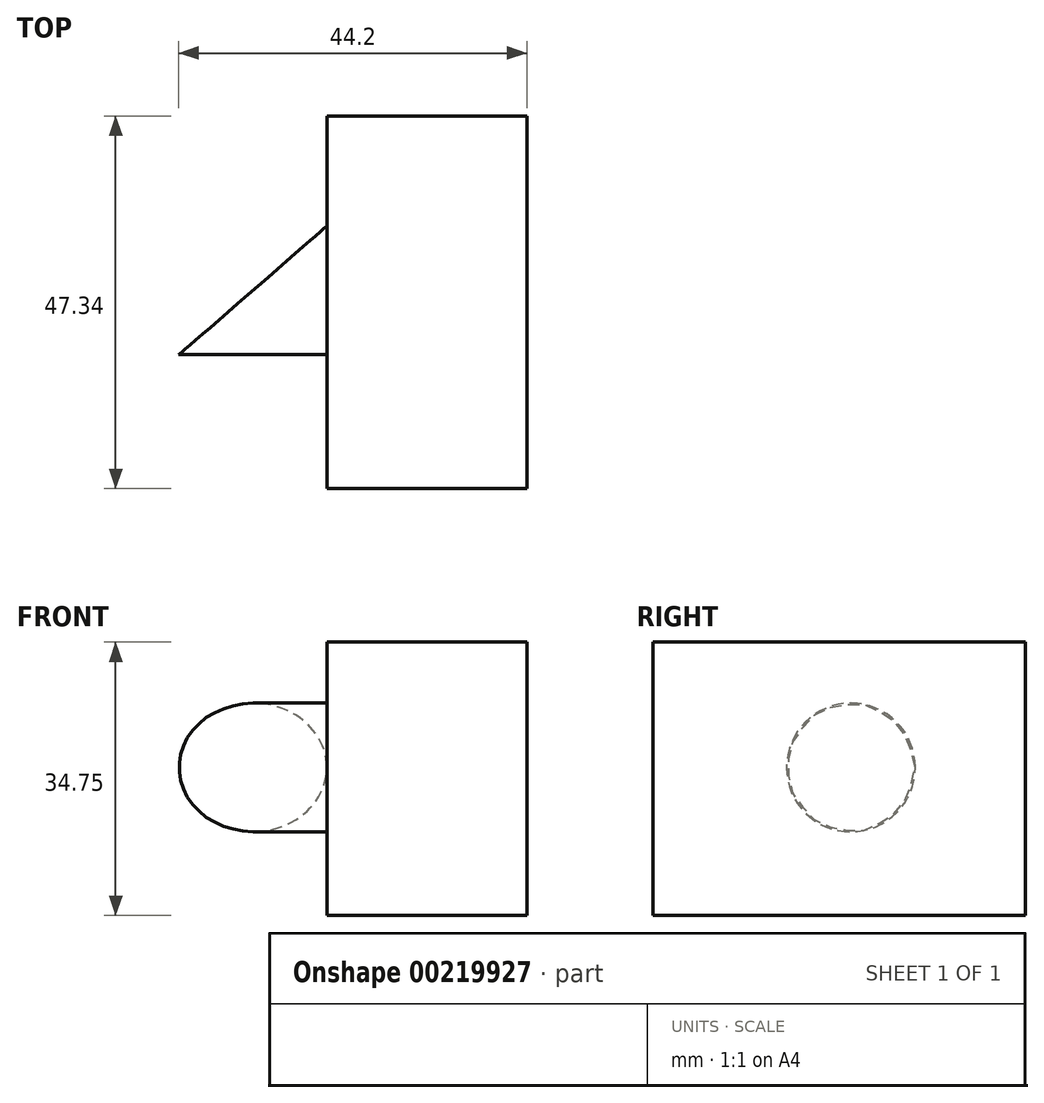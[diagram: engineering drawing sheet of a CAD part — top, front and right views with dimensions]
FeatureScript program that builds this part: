
annotation { "Feature Type Name" : "Feature", "Feature Type Description" : "" }
export const myFeature = defineFeature(function(context is Context, id is Id, definition is map)
    precondition{}
    {
        {
            var Q0;
            Q0=qCreatedBy(makeId("Right.planeOp"),FACE);
            var sketch = newSketch(context, id + "F0", { "sketchPlane" : qUnion([Q0])});
            skLineSegment(sketch, "E0", {"start": v(0, 0) * mm, "end": v(0, 34.75) * mm});
            skLineSegment(sketch, "E1", {"start": v(0, 34.75) * mm, "end": v(47.34, 34.75) * mm});
            skLineSegment(sketch, "E2", {"start": v(47.34, 34.75) * mm, "end": v(47.34, 0) * mm});
            skLineSegment(sketch, "E3", {"start": v(0, 0) * mm, "end": v(47.34, 0) * mm});
            skSolve(sketch);
        }
        {
            var Q0;
            Q0=makeQuery(id+"F0.imprint","IMPRINT",FACE,{"disambiguationData":[TD([[makeQuery(id+"F0.imprint","IMPRINT",EDGE,{"derivedFrom":sQuery(id+"F0.wireOp",EDGE,"E0")}),-1.0]])]});
            extrude(context, id + "F1", {"entities" : qUnion([Q0]), "depth" : 25.4 * mm});
        }
        {
            var Q0;
            Q0=makeQuery(id+"F1.opExtrude","CAP_FACE",FACE,{"disambiguationData":[OSD([sQuery(id+"F0.wireOp",EDGE,"E0"),sQuery(id+"F0.wireOp",EDGE,"E1"),sQuery(id+"F0.wireOp",EDGE,"E2"),sQuery(id+"F0.wireOp",EDGE,"E3")])],"isStart":true});
            var sketch = newSketch(context, id + "F2", { "sketchPlane" : qUnion([Q0])});
            skCircle(sketch, "E4", {"center": v(-25.17, 18.82) * mm, "radius": 8.17 * mm});
            skSolve(sketch);
        }
        {
            var Q0;
            Q0=makeQuery(id+"F2.imprint","IMPRINT",FACE,{"disambiguationData":[TD([[makeQuery(id+"F2.imprint","IMPRINT",EDGE,{"derivedFrom":sQuery(id+"F2.wireOp",EDGE,"E4")}),1.0]])]});
            extrude(context, id + "F3", {"entities" : qUnion([Q0]), "operationType" : NewBodyOperationType.ADD, "depth" : 18.8 * mm});
        }
        {
            var Q0;
            Q0=makeQuery(id+"F1.opExtrude","SWEPT_FACE",FACE,{"disambiguationData":[OSD([sQuery(id+"F0.wireOp",EDGE,"E1")])]});
            var sketch = newSketch(context, id + "F4", { "sketchPlane" : qUnion([Q0])});
            skLineSegment(sketch, "E5", {"start": v(-18.8, 33.34) * mm, "end": v(0, 33.34) * mm});
            skLineSegment(sketch, "E6.0", {"start": v(-18.8, 17) * mm, "end": v(-18.8, 33.34) * mm});
            skLineSegment(sketch, "E7", {"start": v(-18.8, 17) * mm, "end": v(0, 33.34) * mm});
            skSolve(sketch);
        }
        {
            var Q0;
            Q0 = qSketchRegion(id + "F4", true);
            extrude(context, id + "F5", {"entities" : qUnion([Q0]), "operationType" : NewBodyOperationType.REMOVE, "endBound" : BoundingType.THROUGH_ALL, "oppositeDirection" : true, "depth" : 25.4 * mm});
        }
    });
